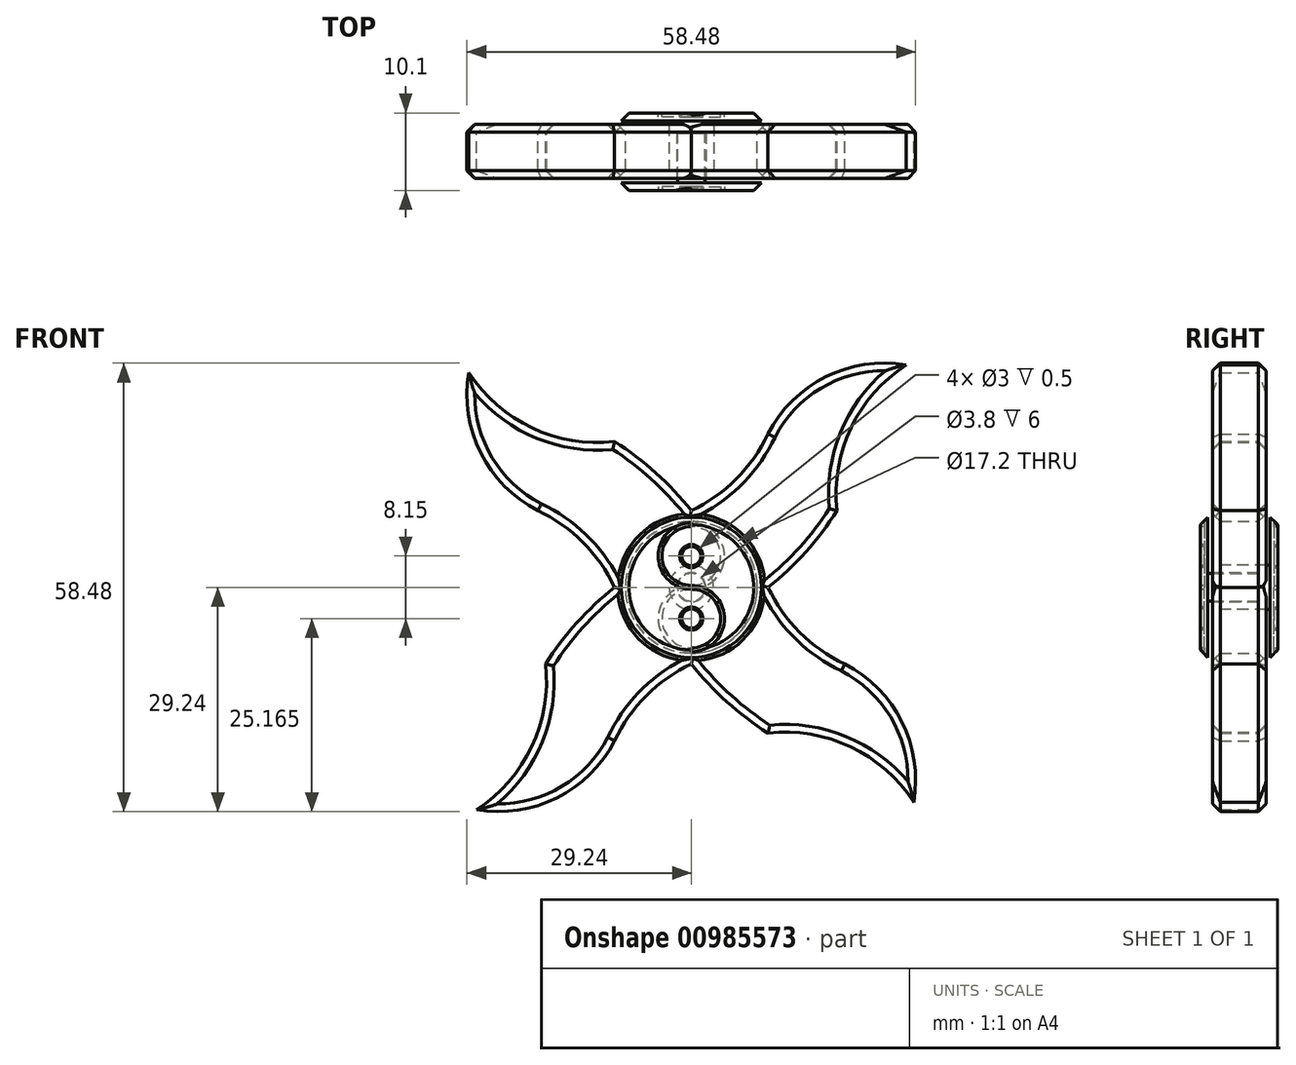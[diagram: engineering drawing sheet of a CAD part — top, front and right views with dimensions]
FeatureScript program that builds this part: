
annotation { "Feature Type Name" : "Feature", "Feature Type Description" : "" }
export const myFeature = defineFeature(function(context is Context, id is Id, definition is map)
    precondition{}
    {
        {
            var Q0;
            Q0=qCreatedBy(makeId("Front.planeOp"),FACE);
            var sketch = newSketch(context, id + "F0", { "sketchPlane" : qUnion([Q0])});
            skCircle(sketch, "E0", {"center": v(0, 0) * mm, "radius": 8.6 * mm});
            skLineSegment(sketch, "E1.bottom", {"start": v(10, 10) * mm, "end": v(-10, 10) * mm});
            skLineSegment(sketch, "E1.top", {"start": v(10, -10) * mm, "end": v(-10, -10) * mm});
            skLineSegment(sketch, "E1.left", {"start": v(10, 10) * mm, "end": v(10, -10) * mm});
            skLineSegment(sketch, "E1.right", {"start": v(-10, 10) * mm, "end": v(-10, -10) * mm});
            skArc(sketch, "E2", {"start": v(0, 10) * mm, "mid": v(5.87, 14.13) * mm, "end": v(10, 20) * mm});
            skArc(sketch, "E3", {"start": v(10, 0) * mm, "mid": v(14.92, 4.62) * mm, "end": v(19, 10) * mm});
            skArc(sketch, "E4", {"start": v(28, 29) * mm, "mid": v(17.53, 27.45) * mm, "end": v(10, 20) * mm});
            skArc(sketch, "E5", {"start": v(28, 29) * mm, "mid": v(20.8, 20.78) * mm, "end": v(19, 10) * mm});
            skLineSegment(sketch, "E6", {"start": v(0, 10) * mm, "end": v(0, -10) * mm, "construction": true});
            skLineSegment(sketch, "E7", {"start": v(10, 0) * mm, "end": v(-10, 0) * mm, "construction": true});
            skArc(sketch, "E8.1.0", {"start": v(-29, 28) * mm, "mid": v(-27.45, 17.53) * mm, "end": v(-20, 10) * mm});
            skArc(sketch, "E8.1.1", {"start": v(-29, 28) * mm, "mid": v(-20.78, 20.8) * mm, "end": v(-10, 19) * mm});
            skArc(sketch, "E8.1.2", {"start": v(0, 10) * mm, "mid": v(-4.62, 14.92) * mm, "end": v(-10, 19) * mm});
            skArc(sketch, "E8.1.3", {"start": v(-10, 0) * mm, "mid": v(-14.13, 5.87) * mm, "end": v(-20, 10) * mm});
            skArc(sketch, "E8.2.0", {"start": v(-28, -29) * mm, "mid": v(-17.53, -27.45) * mm, "end": v(-10, -20) * mm});
            skArc(sketch, "E8.2.1", {"start": v(-28, -29) * mm, "mid": v(-20.8, -20.78) * mm, "end": v(-19, -10) * mm});
            skArc(sketch, "E8.2.2", {"start": v(-10, 0) * mm, "mid": v(-14.92, -4.62) * mm, "end": v(-19, -10) * mm});
            skArc(sketch, "E8.2.3", {"start": v(0, -10) * mm, "mid": v(-5.87, -14.13) * mm, "end": v(-10, -20) * mm});
            skArc(sketch, "E8.3.0", {"start": v(29, -28) * mm, "mid": v(27.45, -17.53) * mm, "end": v(20, -10) * mm});
            skArc(sketch, "E8.3.1", {"start": v(29, -28) * mm, "mid": v(20.78, -20.8) * mm, "end": v(10, -19) * mm});
            skArc(sketch, "E8.3.2", {"start": v(0, -10) * mm, "mid": v(4.62, -14.92) * mm, "end": v(10, -19) * mm});
            skArc(sketch, "E8.3.3", {"start": v(10, 0) * mm, "mid": v(14.13, -5.87) * mm, "end": v(20, -10) * mm});
            skSolve(sketch);
        }
        {
            var Q0;
            {var subQ0=sQuery(id+"F0.wireOp",EDGE,"Vp6JBerj-jvqx-wteG-BcA9-AdoLIlHuIIgN");Q0=makeQuery(id+"F0.imprint","IMPRINT",FACE,{"disambiguationData":[TD([[makeQuery(id+"F0.imprint","IMPRINT",EDGE,{"derivedFrom":subQ0}),1.0]])]});}
            var Q1;
            {var subQ0=sQuery(id+"F0.wireOp",EDGE,"LdxYm28s-e4po-OZL6-0971-FUMEBrMGIPo1");Q1=makeQuery(id+"F0.imprint","IMPRINT",FACE,{"disambiguationData":[TD([[makeQuery(id+"F0.imprint","IMPRINT",EDGE,{"derivedFrom":subQ0}),-1.0]])]});}
            var Q2;
            {var subQ0=sQuery(id+"F0.wireOp",EDGE,"808749d7-399f-4536-bc63-b0ac97090018.1.5");Q2=makeQuery(id+"F0.imprint","IMPRINT",FACE,{"disambiguationData":[TD([[makeQuery(id+"F0.imprint","IMPRINT",EDGE,{"derivedFrom":subQ0}),1.0]])]});}
            var Q3;
            Q3=makeQuery(id+"F0.imprint","IMPRINT",FACE,{"disambiguationData":[TD([[makeQuery(id+"F0.imprint","IMPRINT",EDGE,{"derivedFrom":sQuery(id+"F0.wireOp",EDGE,"eaeeb1f4-a0e6-446a-8670-cc959748b59a.1")}),1.0]])]});
            var Q4;
            Q4=makeQuery(id+"F0.imprint","IMPRINT",FACE,{"disambiguationData":[TD([[makeQuery(id+"F0.imprint","IMPRINT",EDGE,{"derivedFrom":sQuery(id+"F0.wireOp",EDGE,"E0")}),-1.0]])]});
            var Q5;
            Q5=makeQuery(id+"F0.imprint","IMPRINT",FACE,{"disambiguationData":[TD([[makeQuery(id+"F0.imprint","IMPRINT",EDGE,{"derivedFrom":sQuery(id+"F0.wireOp",EDGE,"eaeeb1f4-a0e6-446a-8670-cc959748b59a.0")}),-1.0]])]});
            extrude(context, id + "F1", {"entities" : qUnion([Q0, Q1, Q2, Q3, Q4, Q5]), "depth" : 7 * mm, "offsetDistance" : 25 * mm});
        }
        {
            var Q0;
            Q0=qCreatedBy(makeId("Top.planeOp"),FACE);
            var sketch = newSketch(context, id + "F2", { "sketchPlane" : qUnion([Q0])});
            skPoint(sketch, "E9.0", {"position": v(0, 0) * mm});
            skLineSegment(sketch, "E10", {"start": v(0, 0) * mm, "end": v(-2.9, 0) * mm, "construction": true});
            skLineSegment(sketch, "E11", {"start": v(-2.9, 0) * mm, "end": v(-2.9, -7) * mm});
            skLineSegment(sketch, "E12", {"start": v(-9.15, 1.5) * mm, "end": v(-9.15, 0.5) * mm});
            skLineSegment(sketch, "E13", {"start": v(-9.15, 0.5) * mm, "end": v(-2.9, 0.5) * mm});
            skLineSegment(sketch, "E14", {"start": v(-2.9, 0.5) * mm, "end": v(-2.9, 0) * mm});
            skLineSegment(sketch, "E15", {"start": v(-2.9, -7) * mm, "end": v(-1.9, -7) * mm});
            skLineSegment(sketch, "E16", {"start": v(-1.9, -7) * mm, "end": v(-1.9, -1) * mm});
            skLineSegment(sketch, "E17", {"start": v(-1.9, -1) * mm, "end": v(0, -1) * mm});
            skLineSegment(sketch, "E18", {"start": v(0, -1) * mm, "end": v(0, 1.5) * mm});
            skLineSegment(sketch, "E19", {"start": v(0, 1.5) * mm, "end": v(-9.15, 1.5) * mm});
            skSolve(sketch);
        }
        {
            var Q0;
            Q0=makeQuery(id+"F2.imprint","IMPRINT",FACE,{"disambiguationData":[TD([[makeQuery(id+"F2.imprint","IMPRINT",EDGE,{"derivedFrom":sQuery(id+"F2.wireOp",EDGE,"E11")}),1.0]])]});
            var Q1;
            Q1=sQuery(id+"F2.wireOp",EDGE,"E18");
            revolve(context, id + "F3", {"surfaceOperationType" : NewSurfaceOperationType.NEW, "entities" : qUnion([Q0]), "axis" : qUnion([Q1]), "revolveType" : RevolveType.FULL});
        }
        {
            var Q0;
            Q0=makeQuery(id+"F3.opRevolve","SWEPT_EDGE",EDGE,{"disambiguationData":[OSD([sQuery(id+"F2.wireOp",EDGE,"E12"),sQuery(id+"F2.wireOp",EDGE,"E19")])]});
            chamfer(context, id + "F4", {"entities" : qUnion([Q0]), "width" : 1 * mm, "tangentPropagation" : true});
        }
        {
            var Q0;
            Q0=qCreatedBy(makeId("Top.planeOp"),FACE);
            var sketch = newSketch(context, id + "F5", { "sketchPlane" : qUnion([Q0])});
            skLineSegment(sketch, "E20", {"start": v(0, 0) * mm, "end": v(0, -9.33) * mm, "construction": true});
            skLineSegment(sketch, "E21.0", {"start": v(1.9, -7) * mm, "end": v(-1.9, -7) * mm});
            skLineSegment(sketch, "E22", {"start": v(0, -7) * mm, "end": v(-1.9, -7) * mm});
            skLineSegment(sketch, "E23", {"start": v(-1.9, -7) * mm, "end": v(-1.8, -7) * mm, "construction": true});
            skLineSegment(sketch, "E24", {"start": v(-1.8, -7) * mm, "end": v(-1.8, -1.1) * mm});
            skLineSegment(sketch, "E25", {"start": v(-1.8, -1.1) * mm, "end": v(0, -1.1) * mm});
            skLineSegment(sketch, "E26", {"start": v(0, -1.1) * mm, "end": v(0, -8.6) * mm});
            skLineSegment(sketch, "E27", {"start": v(0, -8.6) * mm, "end": v(-9.15, -8.6) * mm});
            skLineSegment(sketch, "E28", {"start": v(-9.15, -8.6) * mm, "end": v(-9.15, -7.6) * mm});
            skLineSegment(sketch, "E29", {"start": v(-9.15, -7.6) * mm, "end": v(-1.8, -7.6) * mm});
            skLineSegment(sketch, "E30", {"start": v(-1.8, -7.6) * mm, "end": v(-1.8, -7) * mm});
            skSolve(sketch);
        }
        {
            var Q0;
            {var subQ3=sQuery(id+"F5.wireOp",EDGE,"E27");Q0=makeQuery(id+"F5.imprint","IMPRINT",FACE,{"disambiguationData":[TD([[makeQuery(id+"F5.imprint","IMPRINT",EDGE,{"derivedFrom":subQ3}),-1.0]])]});}
            var Q1;
            {var subQ3=sQuery(id+"F5.wireOp",EDGE,"E24");Q1=makeQuery(id+"F5.imprint","IMPRINT",FACE,{"disambiguationData":[TD([[makeQuery(id+"F5.imprint","IMPRINT",EDGE,{"derivedFrom":subQ3}),-1.0]])]});}
            var Q2;
            Q2=sQuery(id+"F5.wireOp",EDGE,"E26");
            revolve(context, id + "F6", {"operationType" : NewBodyOperationType.ADD, "surfaceOperationType" : NewSurfaceOperationType.NEW, "entities" : qUnion([Q0, Q1]), "axis" : qUnion([Q2]), "revolveType" : RevolveType.FULL});
        }
        {
            var Q0;
            Q0=makeQuery(id+"F6.opRevolve","SWEPT_EDGE",EDGE,{"disambiguationData":[OSD([sQuery(id+"F5.wireOp",EDGE,"E27"),sQuery(id+"F5.wireOp",EDGE,"E28")])]});
            chamfer(context, id + "F7", {"entities" : qUnion([Q0]), "width" : 1 * mm, "tangentPropagation" : true});
        }
        {
            var Q0;
            Q0=makeQuery(id+"F0.imprint","IMPRINT",FACE,{"disambiguationData":[TD([[makeQuery(id+"F0.imprint","IMPRINT",EDGE,{"derivedFrom":sQuery(id+"F0.wireOp",EDGE,"E8.1.0")}),1.0]])]});
            var Q1;
            Q1=makeQuery(id+"F0.imprint","IMPRINT",FACE,{"disambiguationData":[TD([[makeQuery(id+"F0.imprint","IMPRINT",EDGE,{"derivedFrom":sQuery(id+"F0.wireOp",EDGE,"E0")}),-1.0]])]});
            var Q2;
            {var subQ0=sQuery(id+"F0.wireOp",EDGE,"E2");Q2=makeQuery(id+"F0.imprint","IMPRINT",FACE,{"disambiguationData":[TD([[makeQuery(id+"F0.imprint","IMPRINT",EDGE,{"derivedFrom":subQ0}),-1.0]])]});}
            var Q3;
            Q3=makeQuery(id+"F0.imprint","IMPRINT",FACE,{"disambiguationData":[TD([[makeQuery(id+"F0.imprint","IMPRINT",EDGE,{"derivedFrom":sQuery(id+"F0.wireOp",EDGE,"E8.3.0")}),1.0]])]});
            var Q4;
            Q4=makeQuery(id+"F0.imprint","IMPRINT",FACE,{"disambiguationData":[TD([[makeQuery(id+"F0.imprint","IMPRINT",EDGE,{"derivedFrom":sQuery(id+"F0.wireOp",EDGE,"E8.2.0")}),1.0]])]});
            extrude(context, id + "F8", {"entities" : qUnion([Q0, Q1, Q2, Q3, Q4]), "operationType" : NewBodyOperationType.ADD, "depth" : 7 * mm, "offsetDistance" : 25 * mm});
        }
        {
            var Q0;
            {var subQ0=sQuery(id+"F0.wireOp",EDGE,"E0");Q0=makeQuery(id+"F8.boolean.opBoolean","MERGE",FACE,{"derivedFrom":[makeQuery(id+"F1.opExtrude","CAP_FACE",FACE,{"disambiguationData":[OSD([subQ0,sQuery(id+"F0.wireOp",EDGE,"E1.bottom"),sQuery(id+"F0.wireOp",EDGE,"E1.top"),sQuery(id+"F0.wireOp",EDGE,"E1.left"),sQuery(id+"F0.wireOp",EDGE,"E1.right")])],"isStart":false}),makeQuery(id+"F8.opExtrude","CAP_FACE",FACE,{"disambiguationData":[OSD([subQ0,sQuery(id+"F0.wireOp",EDGE,"E2"),sQuery(id+"F0.wireOp",EDGE,"E3"),sQuery(id+"F0.wireOp",EDGE,"E4"),sQuery(id+"F0.wireOp",EDGE,"E5"),sQuery(id+"F0.wireOp",EDGE,"E8.1.0"),sQuery(id+"F0.wireOp",EDGE,"E8.1.1"),sQuery(id+"F0.wireOp",EDGE,"E8.1.2"),sQuery(id+"F0.wireOp",EDGE,"E8.1.3"),sQuery(id+"F0.wireOp",EDGE,"E8.2.0"),sQuery(id+"F0.wireOp",EDGE,"E8.2.1"),sQuery(id+"F0.wireOp",EDGE,"E8.2.2"),sQuery(id+"F0.wireOp",EDGE,"E8.2.3"),sQuery(id+"F0.wireOp",EDGE,"E8.3.0"),sQuery(id+"F0.wireOp",EDGE,"E8.3.1"),sQuery(id+"F0.wireOp",EDGE,"E8.3.2"),sQuery(id+"F0.wireOp",EDGE,"E8.3.3")])],"isStart":false})]});}
            chamfer(context, id + "F9", {"entities" : qUnion([Q0]), "width" : 1 * mm, "tangentPropagation" : true});
        }
        {
            var Q0;
            {var subQ0=sQuery(id+"F0.wireOp",EDGE,"E0");Q0=makeQuery(id+"F8.boolean.opBoolean","MERGE",FACE,{"derivedFrom":[makeQuery(id+"F1.opExtrude","CAP_FACE",FACE,{"disambiguationData":[OSD([subQ0,sQuery(id+"F0.wireOp",EDGE,"E1.bottom"),sQuery(id+"F0.wireOp",EDGE,"E1.top"),sQuery(id+"F0.wireOp",EDGE,"E1.left"),sQuery(id+"F0.wireOp",EDGE,"E1.right")])],"isStart":true}),makeQuery(id+"F8.opExtrude","CAP_FACE",FACE,{"disambiguationData":[OSD([subQ0,sQuery(id+"F0.wireOp",EDGE,"E2"),sQuery(id+"F0.wireOp",EDGE,"E3"),sQuery(id+"F0.wireOp",EDGE,"E4"),sQuery(id+"F0.wireOp",EDGE,"E5"),sQuery(id+"F0.wireOp",EDGE,"E8.1.0"),sQuery(id+"F0.wireOp",EDGE,"E8.1.1"),sQuery(id+"F0.wireOp",EDGE,"E8.1.2"),sQuery(id+"F0.wireOp",EDGE,"E8.1.3"),sQuery(id+"F0.wireOp",EDGE,"E8.2.0"),sQuery(id+"F0.wireOp",EDGE,"E8.2.1"),sQuery(id+"F0.wireOp",EDGE,"E8.2.2"),sQuery(id+"F0.wireOp",EDGE,"E8.2.3"),sQuery(id+"F0.wireOp",EDGE,"E8.3.0"),sQuery(id+"F0.wireOp",EDGE,"E8.3.1"),sQuery(id+"F0.wireOp",EDGE,"E8.3.2"),sQuery(id+"F0.wireOp",EDGE,"E8.3.3")])],"isStart":true})]});}
            chamfer(context, id + "F10", {"entities" : qUnion([Q0]), "width" : 1 * mm, "tangentPropagation" : true});
        }
        {
            var Q0;
            Q0=makeQuery(id+"F6.opRevolve","SWEPT_FACE",FACE,{"disambiguationData":[OSD([sQuery(id+"F5.wireOp",EDGE,"E27")])]});
            var sketch = newSketch(context, id + "F11", { "sketchPlane" : qUnion([Q0])});
            skLineSegment(sketch, "E31", {"start": v(0, 0) * mm, "end": v(0, 8.15) * mm, "construction": true});
            skArc(sketch, "E32", {"start": v(0, 8.15) * mm, "mid": v(-4.08, 4.08) * mm, "end": v(0, 0) * mm});
            skLineSegment(sketch, "E33", {"start": v(0, 0) * mm, "end": v(0, -8.15) * mm, "construction": true});
            skArc(sketch, "E34", {"start": v(0, -8.15) * mm, "mid": v(4.08, -4.08) * mm, "end": v(0, 0) * mm});
            skCircle(sketch, "E35", {"center": v(0, 4.08) * mm, "radius": 1.5 * mm});
            skCircle(sketch, "E36", {"center": v(0, -4.08) * mm, "radius": 1.5 * mm});
            skArc(sketch, "E37.0", {"start": v(0, -7.9) * mm, "mid": v(3.83, -4.08) * mm, "end": v(0, -0.25) * mm});
            skArc(sketch, "E37.1", {"start": v(0, 8.4) * mm, "mid": v(-4.33, 4.07) * mm, "end": v(0, -0.25) * mm});
            skArc(sketch, "E38.0", {"start": v(0, -8.4) * mm, "mid": v(4.33, -4.08) * mm, "end": v(0, 0.25) * mm});
            skArc(sketch, "E38.1", {"start": v(0, 7.9) * mm, "mid": v(-3.83, 4.07) * mm, "end": v(0, 0.25) * mm});
            skCircle(sketch, "E39.0", {"center": v(0, 4.08) * mm, "radius": 1.25 * mm});
            skCircle(sketch, "E40.0", {"center": v(0, -4.08) * mm, "radius": 1.25 * mm});
            skLineSegment(sketch, "E41", {"start": v(0, 8.4) * mm, "end": v(0, 7.9) * mm});
            skLineSegment(sketch, "E42", {"start": v(0, -7.9) * mm, "end": v(0, -8.4) * mm});
            skSolve(sketch);
        }
        {
            var Q0;
            {var subQ6=sQuery(id+"F11.wireOp",EDGE,"E32");Q0=makeQuery(id+"F11.imprint","IMPRINT",FACE,{"disambiguationData":[TD([[makeQuery(id+"F11.imprint","IMPRINT",EDGE,{"derivedFrom":subQ6}),-1.0]])]});}
            var Q1;
            {var subQ6=sQuery(id+"F11.wireOp",EDGE,"E32");Q1=makeQuery(id+"F11.imprint","IMPRINT",FACE,{"disambiguationData":[TD([[makeQuery(id+"F11.imprint","IMPRINT",EDGE,{"derivedFrom":subQ6}),1.0]])]});}
            var Q2;
            Q2=makeQuery(id+"F11.imprint","IMPRINT",FACE,{"disambiguationData":[TD([[makeQuery(id+"F11.imprint","IMPRINT",EDGE,{"derivedFrom":sQuery(id+"F11.wireOp",EDGE,"E35")}),1.0]])]});
            var Q3;
            Q3=makeQuery(id+"F11.imprint","IMPRINT",FACE,{"disambiguationData":[TD([[makeQuery(id+"F11.imprint","IMPRINT",EDGE,{"derivedFrom":sQuery(id+"F11.wireOp",EDGE,"E36")}),1.0]])]});
            var Q4;
            {var subQ0=sQuery(id+"F11.wireOp",EDGE,"E42");var subQ1=sQuery(id+"F11.wireOp",EDGE,"E38.0");var subQ2=makeQuery(id+"F11.imprint","INTERSECT",VERTEX,{"derivedFrom":[subQ1,subQ0]});Q4=makeQuery(id+"F11.imprint","IMPRINT",FACE,{"disambiguationData":[TD([[makeQuery(id+"F11.imprint","IMPRINT",EDGE,{"disambiguationData":[TD([[subQ2,-1.0]])],"derivedFrom":subQ1}),1.0]])]});}
            var Q5;
            {var subQ0=sQuery(id+"F11.wireOp",EDGE,"E41");var subQ1=sQuery(id+"F11.wireOp",EDGE,"E37.1");var subQ2=makeQuery(id+"F11.imprint","INTERSECT",VERTEX,{"derivedFrom":[subQ1,subQ0]});Q5=makeQuery(id+"F11.imprint","IMPRINT",FACE,{"disambiguationData":[TD([[makeQuery(id+"F11.imprint","IMPRINT",EDGE,{"disambiguationData":[TD([[subQ2,-1.0]])],"derivedFrom":subQ1}),1.0]])]});}
            extrude(context, id + "F12", {"entities" : qUnion([Q0, Q1, Q2, Q3, Q4, Q5]), "operationType" : NewBodyOperationType.REMOVE, "oppositeDirection" : true, "depth" : .5 * mm, "offsetDistance" : 25 * mm});
        }
        {
            var Q0;
            Q0=makeQuery(id+"F3.opRevolve","SWEPT_FACE",FACE,{"disambiguationData":[OSD([sQuery(id+"F2.wireOp",EDGE,"E19")])]});
            var sketch = newSketch(context, id + "F13", { "sketchPlane" : qUnion([Q0])});
            skLineSegment(sketch, "E43", {"start": v(0, 0) * mm, "end": v(0, 8.15) * mm, "construction": true});
            skLineSegment(sketch, "E44", {"start": v(0, 0) * mm, "end": v(0, -8.15) * mm, "construction": true});
            skArc(sketch, "E45", {"start": v(0, 8.15) * mm, "mid": v(-4.08, 4.08) * mm, "end": v(0, 0) * mm});
            skArc(sketch, "E46", {"start": v(0, -8.15) * mm, "mid": v(4.08, -4.08) * mm, "end": v(0, 0) * mm});
            skCircle(sketch, "E47", {"center": v(0, 4.08) * mm, "radius": 1.5 * mm});
            skCircle(sketch, "E48", {"center": v(0, -4.08) * mm, "radius": 1.5 * mm});
            skArc(sketch, "E49.0", {"start": v(0, -8.4) * mm, "mid": v(4.33, -4.08) * mm, "end": v(0, 0.25) * mm});
            skArc(sketch, "E49.1", {"start": v(0, 7.9) * mm, "mid": v(-3.83, 4.07) * mm, "end": v(0, 0.25) * mm});
            skArc(sketch, "E50.0", {"start": v(0, -7.9) * mm, "mid": v(3.83, -4.08) * mm, "end": v(0, -0.25) * mm});
            skArc(sketch, "E50.1", {"start": v(0, 8.4) * mm, "mid": v(-4.33, 4.07) * mm, "end": v(0, -0.25) * mm});
            skCircle(sketch, "E51.0", {"center": v(0, 4.08) * mm, "radius": 1.25 * mm});
            skCircle(sketch, "E52.0", {"center": v(0, -4.08) * mm, "radius": 1.25 * mm});
            skLineSegment(sketch, "E53", {"start": v(0, 7.9) * mm, "end": v(0, 8.4) * mm});
            skLineSegment(sketch, "E54", {"start": v(0, -7.9) * mm, "end": v(0, -8.4) * mm});
            skSolve(sketch);
        }
        {
            var Q0;
            {var subQ5=sQuery(id+"F13.wireOp",EDGE,"E45");Q0=makeQuery(id+"F13.imprint","IMPRINT",FACE,{"disambiguationData":[TD([[makeQuery(id+"F13.imprint","IMPRINT",EDGE,{"derivedFrom":subQ5}),-1.0]])]});}
            var Q1;
            {var subQ3=sQuery(id+"F13.wireOp",EDGE,"E45");Q1=makeQuery(id+"F13.imprint","IMPRINT",FACE,{"disambiguationData":[TD([[makeQuery(id+"F13.imprint","IMPRINT",EDGE,{"derivedFrom":subQ3}),1.0]])]});}
            var Q2;
            Q2=makeQuery(id+"F13.imprint","IMPRINT",FACE,{"disambiguationData":[TD([[makeQuery(id+"F13.imprint","IMPRINT",EDGE,{"derivedFrom":sQuery(id+"F13.wireOp",EDGE,"E47")}),1.0]])]});
            var Q3;
            Q3=makeQuery(id+"F13.imprint","IMPRINT",FACE,{"disambiguationData":[TD([[makeQuery(id+"F13.imprint","IMPRINT",EDGE,{"derivedFrom":sQuery(id+"F13.wireOp",EDGE,"E48")}),1.0]])]});
            var Q4;
            {var subQ0=sQuery(id+"F13.wireOp",EDGE,"E54");var subQ1=sQuery(id+"F13.wireOp",EDGE,"E49.0");var subQ2=makeQuery(id+"F13.imprint","INTERSECT",VERTEX,{"derivedFrom":[subQ1,subQ0]});Q4=makeQuery(id+"F13.imprint","IMPRINT",FACE,{"disambiguationData":[TD([[makeQuery(id+"F13.imprint","IMPRINT",EDGE,{"disambiguationData":[TD([[subQ2,-1.0]])],"derivedFrom":subQ1}),1.0]])]});}
            var Q5;
            {var subQ0=sQuery(id+"F13.wireOp",EDGE,"E53");var subQ1=sQuery(id+"F13.wireOp",EDGE,"E50.1");var subQ2=makeQuery(id+"F13.imprint","INTERSECT",VERTEX,{"derivedFrom":[subQ1,subQ0]});Q5=makeQuery(id+"F13.imprint","IMPRINT",FACE,{"disambiguationData":[TD([[makeQuery(id+"F13.imprint","IMPRINT",EDGE,{"disambiguationData":[TD([[subQ2,-1.0]])],"derivedFrom":subQ1}),1.0]])]});}
            extrude(context, id + "F14", {"entities" : qUnion([Q0, Q1, Q2, Q3, Q4, Q5]), "operationType" : NewBodyOperationType.REMOVE, "oppositeDirection" : true, "depth" : .5 * mm, "offsetDistance" : 25 * mm});
        }
    });
